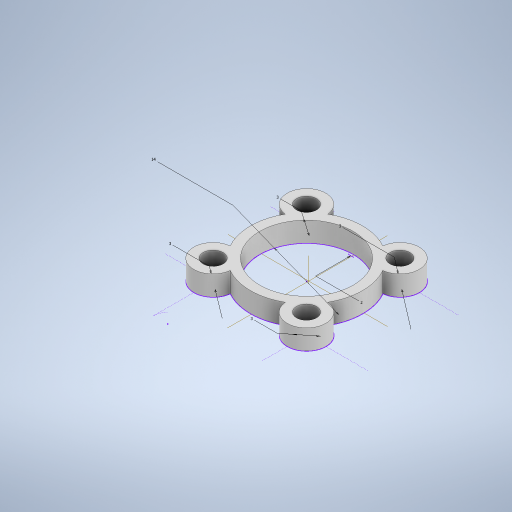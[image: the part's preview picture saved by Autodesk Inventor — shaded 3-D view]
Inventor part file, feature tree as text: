
AUTODESK INVENTOR PART (.ipt)
format: ipt  version: 2024.2 (Build 282272000, 272)  size: 274,432 bytes
history: native  units: mm
features: other x1, sketch x1, extrude x1
ambient origin geometry x8: Origin, YZ Plane, XZ Plane, XY Plane, X Axis, Y Axis, Z Axis, Center Point
bodies: Body1 (feature_tree)
feature tree (3):
  other  "Твердое тело1"
  sketch  "Эскиз1"
  extrude  "Выдавливание1"  Depth=3.0mm TaperAngle=0.0deg
